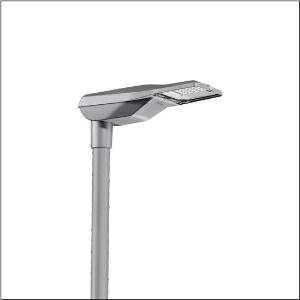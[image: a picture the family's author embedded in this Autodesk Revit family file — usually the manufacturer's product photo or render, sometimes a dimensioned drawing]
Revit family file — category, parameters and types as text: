
# Revit family: streetlight_sl_21_iq_micro___st1_5a_5xe1p31d08cb_2d79
name_source: partatom
category: Lighting Fixtures
units: mm (PartAtom-declared; Revit-internal decimal feet)

## family parameters
Cut with Voids When Loaded = No
Host = Face
Light Source = No
Part Type = Normal
Room Calculation Point = No
Round Connector Dimension = Use Diameter
Shared = No

## types (1)
- --- (1 x LED, 2820 lm, 19.4 W, 3000K)
    Apparent Load = 19 VA
    CIE Flux Codes = 22 53 95 100 100
    Color Rendering = 70
    Color Temperature = 3000K
    Default Elevation = 1800 mm
    Description = Streetlight SL 21 iQ micro, mast luminaire, primary light control with lens, of PMMA, primary optical cover: cover, of toughened safety glass, transparent, light distribution: ST1.5a, light emission: direct distribution, primary light characteristic: asymmetric, installation type: post-top, side-entry, LED, High Power LED, rated luminous flux: 2.820lm, luminous efficacy: 145lm/W, light colour: 730, colour temperature: 3000K, control: Auto-Match, Temp-Guard, Lumen-Switch, Night-Set, Smart-Wire, Light-Fading, Desk-Remote (wireless, voltage-free reading and setting of iQ features in the workshop via application-optimized NFC function/RFID function), optimised constant luminous flux control (CLO 2.0), presetting dimming linear, mains connection: 220..240V, AC, 50/60Hz, start of lifetime: 19W, end of service life: 20W, reduction: 10W, luminaire housing, of diecast aluminium, powder-coated, Siteco® metallic grey (DB 702S), corrosivity category C5 mid according to DIN EN ISO 12944, please order mast flange separately, inclination adjustable: 0°, 5°, 10°, 15°, sealing non-destructively replaceable, multi-level sealing system, length: 528mm, width: 235mm, height: 110mm, mast flange for spigot size: 42mm (side-entry): 5XC10008XM4, 60/48mm (side-entry/post-top): 5XC10108XM2, 76/60mm (side-entry/post-top): 5XC10108XM1, protection rating (complete): IP66, insulation class (complete): insulation class II (safety insulation), certification: CE, ENEC, ENEC+, VDE, impact resistance: IK09, permissible operating ambient temperature for outdoor applications: -40..+50°C, standard-compliant lighting for roads and squares, packaging unit: 1 piece

Light Distribution: ST1.5a
    Height = 110 mm
    Lamp = 1 x LED
    Lamp Light Flux = 2820 lm
    Lamp Power = 19.4 W
    Lamp count = 1
    Length = 528 mm
    Luminous efficacy = 145 lm/W
    Manufacturer = Siteco
    ModVariant = No
    Model = 5XE1P31D08CB
    Number of Poles = 1
    OnlyDefault = Yes
    Power Factor = 1
    Product Name = Streetlight SL 21 iQ micro | ST1.5a
    Product group = mast luminaire | pylon top
    ProductGroupID = 6100
    Protection Class = Protection class II
    Protection Degree = IP 66
    RLX_Detail_Level = 1
    RLX_Emergency_Light_Flux = 0 lm
    RLX_Emergency_Type = 0
    RLX_Emergency_Type_DB = No
    RlxData = <blob elided: 102977 chars, md5=c0f7b506>
    Socket = socket
    Standby Power = 0 W
    System Light Flux = 2820 lm
    System Power = 19 W
    Type Comments = factory setting: luminous flux: 100 % | dim-lin: 254 | 387 mA
    Type Image = l_1006881.jpg
    URL = http://relux.com
    VarID = @adj_069433
    Voltage = 0 V
    Weight = 0.00 kg
    Width = 235 mm

## geometry (parser evidence)
native form markers: Blend x4, Sweep x12
no freeform markers — native parametric forms only
